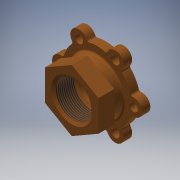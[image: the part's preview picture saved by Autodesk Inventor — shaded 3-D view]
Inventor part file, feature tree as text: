
AUTODESK INVENTOR PART (.ipt)
format: ipt  version: 2018 (Build 220112000, 112)  size: 287,232 bytes
history: native  units: mm (DEFAULTED — no unit token found)
features: sketch x4, fillet x2, extrude x2, revolve x1, thread x1, hole x1, pattern_circular x1
ambient origin geometry x8: Origin, YZ Plane, XZ Plane, XY Plane, X Axis, Y Axis, Z Axis, Center Point
bodies: Solid1 (feature_tree)
feature tree (12):
  revolve  "Revolution1"  [1 undecoded]
  fillet  "Fillet1"  Radius=38.0mm
  extrude  "Extrusion1"  Depth=57.0mm
  thread  "Thread1"  [1 undecoded]
  extrude  "Extrusion2"  Depth=57.0mm
  fillet  "Fillet2"  Radius=5.0mm
  hole  "Hole1"  [1 undecoded]
  pattern_circular  "Circular Pattern1"  [2 undecoded]
  sketch  "Sketch1"  dims[d0=3.0mm d1=32.0mm d2=38.0mm]
  sketch  "Sketch2"  dims[d3=57.0mm d4=40.0mm d5=51.0mm]
  sketch  "Sketch3"  dims[d6=57.0mm d7=74.0mm d8=5.0mm]
  sketch  "Sketch4"  dims[d9=2.0mm d10=21.0mm d11=23.0mm d12=26.0mm d13=29.0mm d14=27.0mm d15=33.0mm d16=36.0mm d17=39.0mm d18=90.0deg d19=2.0mm d20=17.0mm d21=0.0mm d22=10.0mm d23=0.0mm d24=9.0mm d25=78.0mm d26=9.0mm d27=0.0mm d28=2.0mm d29=9.0mm d30=6.0mm d31=4.0mm d32=2.0mm d33=14.3117mm d34=8.0mm d35=20.594885mm d36=60.0mm d38=360.0deg]
note: 5 required parameter values undecoded (feature->parameter linkage not recoverable at this tier; creation-order binding heuristic only, values carry confidence <= 0.55)